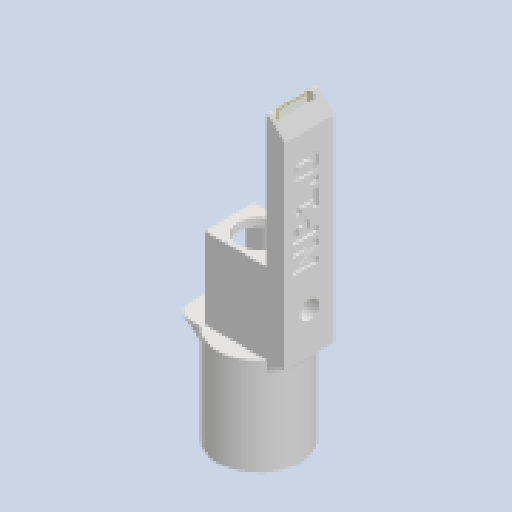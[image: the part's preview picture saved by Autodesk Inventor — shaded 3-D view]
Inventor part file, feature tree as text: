
AUTODESK INVENTOR PART (.ipt)
format: ipt  version: 2023 (Build 270158000, 158)  size: 456,192 bytes
history: native  units: in
note: dims shown in document units (in); Inventor stores cm internally (conversion verified against a paired STEP export)
features: extrude x13, sketch x11, reference x9, fillet x5, other x4, projected_geometry x2, plane x1, chamfer x1, emboss x1
ambient origin geometry x8: Origin, YZ Plane, XZ Plane, XY Plane, X Axis, Y Axis, Z Axis, Center Point
bodies: Solid1 (feature_tree)
feature tree (47):
  plane  "Work Plane2"
  extrude  "arm_base"  Depth=0.0394in
  extrude  "arm_tabs"  Depth=0.0079in
  extrude  "cut_out"  Depth=0.0295in TaperAngle=0.0deg
  chamfer  "Chamfer1"  Distance=0.5906in
  extrude  "slider_box"  Depth=0.3031in TaperAngle=0.0deg
  extrude  "slider_cutout"  Depth=0.3031in TaperAngle=0.0deg
  extrude  "cylinder_post"  Depth=0.4724in TaperAngle=0.0deg
  fillet  "Fillet2"  Radius=0.0709in
  extrude  "post_cutout"  Depth=0.3543in TaperAngle=0.0deg
  extrude  "well"  Depth=0.315in TaperAngle=0.0deg
  fillet  "Fillet4"  Radius=0.0787in
  sketch  "Sketch32"  dims[d103=0.4016in d104=0.4724in d105=0.0in d107=0.0709in]
  extrude  "side_tab"  Depth=0.0079in TaperAngle=0.0deg
  fillet  "Fillet5"  Radius=0.0787in
  fillet  "Fillet6"  Radius=0.0787in
  extrude  "fill_gaps"  Depth=0.2835in TaperAngle=0.0deg
  extrude  "screw_hole"  Depth=0.0118in
  fillet  "Fillet7"  Radius=0.1291in
  extrude  "screw_hole_2"  Depth=0.0118in
  extrude  "screw_hole_3"  TaperAngle=0.0deg  [1 undecoded]
  emboss  "Emboss1"
  sketch  "Sketch2"  dims[d3=0.0591in d4=0.0in d81=0.0394in]
  reference  "Reference25"
  reference  "Reference26"
  reference  "Reference27"
  reference  "Reference28"
  sketch  "Sketch22"  dims[d82=0.0394in d83=0.0079in]
  reference  "Reference29"
  reference  "Reference30"
  projected_geometry  "Projected Loop3"
  sketch  "Sketch26"  dims[d84=0.0079in d85=0.0295in d86=0.0in d88=0.5906in d89=0.0in]
  projected_geometry  "Projected Loop4"
  sketch  "Sketch28"  dims[d92=0.0787in d93=0.0787in d94=45.0deg d95=0.3031in d96=0.0in]
  sketch  "Sketch29"  dims[d97=0.0394in d101=0.3031in d102=0.0in]
  reference  "Reference39"
  reference  "Reference40"
  sketch  "Sketch33"  dims[d108=0.3228in d109=0.3543in d110=0.0in]
  sketch  "Sketch36"  dims[d111=0.2283in d112=0.315in d113=0.0in d121=0.0787in]
  sketch  "Sketch37"  dims[d122=0.0906in d126=0.0079in d127=0.0in d128=0.0787in d129=0.0787in]
  sketch  "Sketch38"  dims[d131=0.3937in d132=0.2835in d133=0.0in]
  reference  "Reference44"
  sketch  "Sketch39"  dims[d134=0.3937in d135=0.0in d136=0.0591in d137=0.1291in d138=0.1181in d139=0.0in d140=0.0in d141=0.1969in d142=0.4724in d143=0.0in d145=0.02in d146=0.0079in d147=0.0394in d148=0.0394in d149=0.0394in d150=0.0118in d151=0.0in d44=0.5in d45=0.0344in d46=0.5in d47=0.0344in d106=0.0in d123=0.0in d124=0.0in d125=0.0in d130=0.0344in]
  parser-record x2  (decoder bookkeeping rows leaked as tree rows — omitted from the tree; the rows remain in map.json)
  other  "full_assembly.iam"
  other  "probe_holder:1"
note: 1 required parameter value undecoded (feature->parameter linkage not recoverable at this tier; creation-order binding heuristic only, values carry confidence <= 0.55)
note: 2 file-system paths scrubbed to <path> (originals preserved in map.json)
